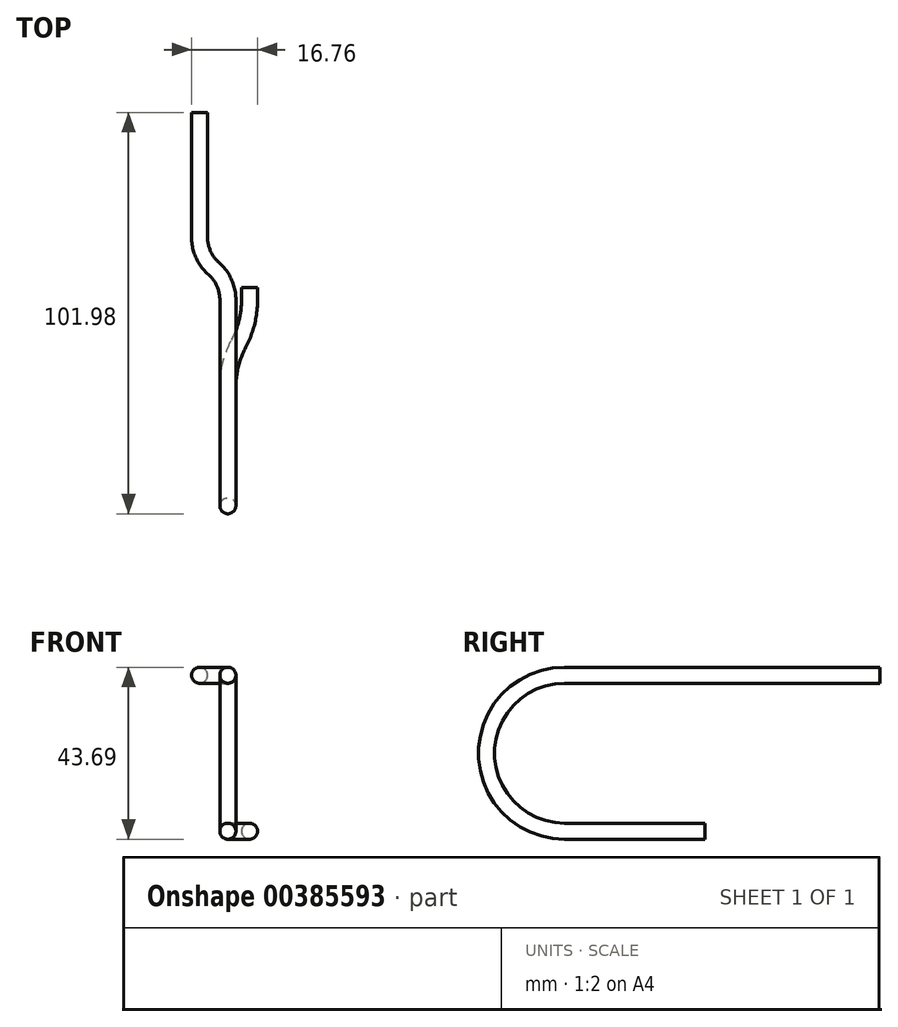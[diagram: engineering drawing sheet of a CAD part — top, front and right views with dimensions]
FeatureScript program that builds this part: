
annotation { "Feature Type Name" : "Feature", "Feature Type Description" : "" }
export const myFeature = defineFeature(function(context is Context, id is Id, definition is map)
    precondition{}
    {
        {
            var Q0;
            Q0=qCreatedBy(makeId("Top.planeOp"),FACE);
            var sketch = newSketch(context, id + "F0", { "sketchPlane" : qUnion([Q0])});
            skPoint(sketch, "E0", {"position": v(0, 0) * mm});
            skPoint(sketch, "E1", {"position": v(-5.51, -25.4) * mm});
            skPoint(sketch, "E2", {"position": v(0, -3.18) * mm});
            skPoint(sketch, "E3", {"position": v(-5.51, -31.75) * mm});
            skLineSegment(sketch, "E4", {"start": v(0, 0) * mm, "end": v(0, -3.18) * mm});
            skLineSegment(sketch, "E5", {"start": v(-5.51, -25.4) * mm, "end": v(-5.51, -31.75) * mm});
            skArc(sketch, "E6", {"start": v(-2.76, -14.29) * mm, "mid": v(-0.7, -8.9) * mm, "end": v(0, -3.18) * mm});
            skArc(sketch, "E7", {"start": v(-2.76, -14.29) * mm, "mid": v(-4.81, -19.68) * mm, "end": v(-5.51, -25.4) * mm});
            skSolve(sketch);
        }
        {
            var Q0;
            Q0=sQuery(id+"F0.wireOp",VERTEX,"E3");
            var Q1;
            Q1=qCreatedBy(makeId("Right.planeOp"),FACE);
            cPlane(context, id + "F1", {"entities" : qUnion([Q0, Q1]), "cplaneType" : CPlaneType.PLANE_POINT, "offset" : 5.5 * mm, "width" : 152.4 * mm, "height" : 152.4 * mm});
        }
        {
            var Q0;
            Q0=qCreatedBy(id+"F1.planeOp",FACE);
            var sketch = newSketch(context, id + "F2", { "sketchPlane" : qUnion([Q0])});
            skPoint(sketch, "E8", {"position": v(-35.69, 0) * mm});
            skPoint(sketch, "E9", {"position": v(-35.69, 39.62) * mm});
            skPoint(sketch, "E10", {"position": v(-6.35, 39.62) * mm});
            skLineSegment(sketch, "E11", {"start": v(-31.75, 0) * mm, "end": v(-35.69, 0) * mm});
            skLineSegment(sketch, "E12", {"start": v(-35.69, 39.62) * mm, "end": v(-6.35, 39.62) * mm});
            skArc(sketch, "E13", {"start": v(-35.69, 39.62) * mm, "mid": v(-55.5, 19.81) * mm, "end": v(-35.69, 0) * mm});
            skSolve(sketch);
        }
        {
            var Q0;
            Q0=qCreatedBy(makeId("Front.planeOp"),FACE);
            var sketch = newSketch(context, id + "F3", { "sketchPlane" : qUnion([Q0])});
            skCircle(sketch, "E14", {"center": v(0, 0) * mm, "radius": 2.03 * mm});
            skSolve(sketch);
        }
        {
            var Q0;
            Q0=qCreatedBy(makeId("Top.planeOp"),FACE);
            var Q1;
            Q1=sQuery(id+"F2.wireOp",VERTEX,"E10");
            cPlane(context, id + "F4", {"entities" : qUnion([Q0, Q1]), "cplaneType" : CPlaneType.PLANE_POINT, "offset" : 25.4 * mm, "width" : 152.4 * mm, "height" : 152.4 * mm});
        }
        {
            var Q0;
            Q0=qCreatedBy(id+"F4.planeOp",FACE);
            var sketch = newSketch(context, id + "F5", { "sketchPlane" : qUnion([Q0])});
            skPoint(sketch, "E15.0", {"position": v(-5.51, -6.35) * mm});
            skPoint(sketch, "E16", {"position": v(-5.51, -3.18) * mm});
            skPoint(sketch, "E17", {"position": v(-12.7, 12.7) * mm});
            skPoint(sketch, "E18", {"position": v(-12.7, 44.45) * mm});
            skLineSegment(sketch, "E19", {"start": v(-5.51, -6.35) * mm, "end": v(-5.51, -3.18) * mm});
            skLineSegment(sketch, "E20", {"start": v(-12.7, 12.7) * mm, "end": v(-12.7, 44.45) * mm});
            skArc(sketch, "E21", {"start": v(-5.51, -3.18) * mm, "mid": v(-6.45, 1.18) * mm, "end": v(-9.1, 4.76) * mm});
            skArc(sketch, "E22", {"start": v(-12.7, 12.7) * mm, "mid": v(-11.76, 8.34) * mm, "end": v(-9.1, 4.76) * mm});
            skSolve(sketch);
        }
        {
            var Q0;
            Q0=makeQuery(id+"F3.imprint","IMPRINT",FACE,{"disambiguationData":[TD([[makeQuery(id+"F3.imprint","IMPRINT",EDGE,{"derivedFrom":sQuery(id+"F3.wireOp",EDGE,"E14")}),1.0]])]});
            var Q1;
            Q1=sQuery(id+"F0.wireOp",EDGE,"E4");
            var Q2;
            Q2=sQuery(id+"F0.wireOp",EDGE,"E6");
            var Q3;
            Q3=sQuery(id+"F0.wireOp",EDGE,"E7");
            var Q4;
            Q4=sQuery(id+"F0.wireOp",EDGE,"E5");
            var Q5;
            Q5=sQuery(id+"F2.wireOp",EDGE,"E11");
            var Q6;
            Q6=sQuery(id+"F2.wireOp",EDGE,"E13");
            var Q7;
            Q7=sQuery(id+"F2.wireOp",EDGE,"E12");
            var Q8;
            Q8=sQuery(id+"F5.wireOp",EDGE,"E19");
            var Q9;
            Q9=sQuery(id+"F5.wireOp",EDGE,"E21");
            var Q10;
            Q10=sQuery(id+"F5.wireOp",EDGE,"E22");
            var Q11;
            Q11=sQuery(id+"F5.wireOp",EDGE,"E20");
            sweep(context, id + "F6", {"profiles" : qUnion([Q0]), "path" : qUnion([Q1, Q2, Q3, Q4, Q5, Q6, Q7, Q8, Q9, Q10, Q11])});
        }
    });
